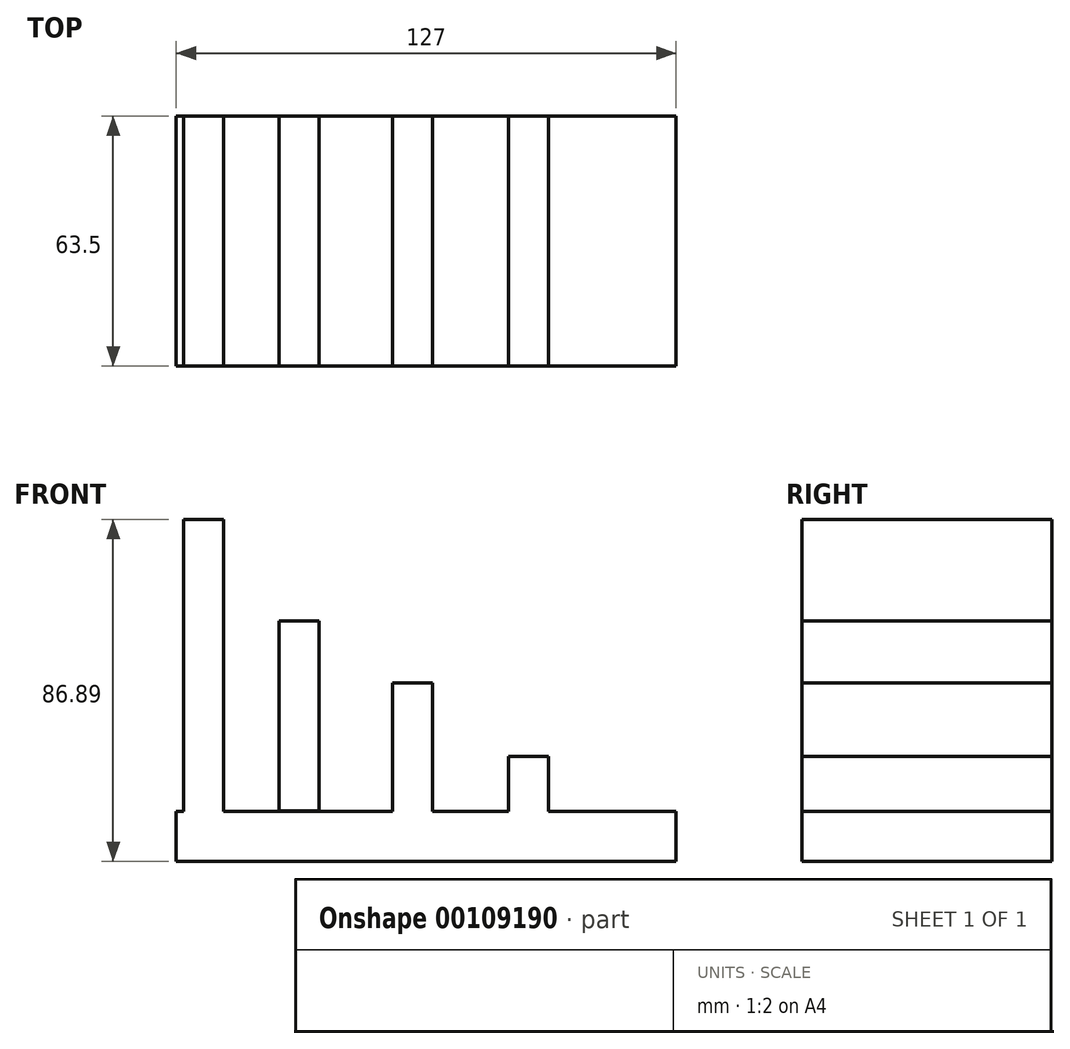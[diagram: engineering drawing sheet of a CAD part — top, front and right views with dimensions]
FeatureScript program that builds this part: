
annotation { "Feature Type Name" : "Feature", "Feature Type Description" : "" }
export const myFeature = defineFeature(function(context is Context, id is Id, definition is map)
    precondition{}
    {
        {
            var Q0;
            Q0=qCreatedBy(makeId("Front.planeOp"),FACE);
            var sketch = newSketch(context, id + "F0", { "sketchPlane" : qUnion([Q0])});
            skLineSegment(sketch, "E0.bottom", {"start": v(-60.38, -31.27) * mm, "end": v(66.62, -31.27) * mm});
            skLineSegment(sketch, "E0.top", {"start": v(-60.38, -43.97) * mm, "end": v(66.62, -43.97) * mm});
            skLineSegment(sketch, "E0.left", {"start": v(-60.38, -31.27) * mm, "end": v(-60.38, -43.97) * mm});
            skLineSegment(sketch, "E0.right", {"start": v(66.62, -31.27) * mm, "end": v(66.62, -43.97) * mm});
            skSolve(sketch);
        }
        {
            var Q0;
            Q0=qCreatedBy(makeId("Front.planeOp"),FACE);
            var sketch = newSketch(context, id + "F1", { "sketchPlane" : qUnion([Q0])});
            skLineSegment(sketch, "E1.bottom", {"start": v(-58.53, -33.29) * mm, "end": v(-48.37, -33.29) * mm});
            skLineSegment(sketch, "E1.top", {"start": v(-58.53, 42.92) * mm, "end": v(-48.37, 42.92) * mm});
            skLineSegment(sketch, "E1.left", {"start": v(-58.53, -33.29) * mm, "end": v(-58.53, 42.92) * mm});
            skLineSegment(sketch, "E1.right", {"start": v(-48.37, -33.29) * mm, "end": v(-48.37, 42.92) * mm});
            skFitSpline(sketch, "E2", {"points": [v(-48.37, 42.92) * mm, v(53.2, -35.52) * mm], "startDerivative": vector(74.92, -128.75) * mm, "endDerivative": vector(141.8, -32.15) * mm});
            skSolve(sketch);
        }
        {
            var Q0;
            Q0=makeQuery(id+"F0.imprint","IMPRINT",FACE,{"disambiguationData":[TD([[makeQuery(id+"F0.imprint","IMPRINT",EDGE,{"derivedFrom":sQuery(id+"F0.wireOp",EDGE,"E0.bottom")}),-1.0]])]});
            extrude(context, id + "F2", {"entities" : qUnion([Q0]), "depth" : 63.5 * mm});
        }
        {
            var Q0;
            Q0=makeQuery(id+"F1.imprint","IMPRINT",FACE,{"disambiguationData":[TD([[makeQuery(id+"F1.imprint","IMPRINT",EDGE,{"derivedFrom":sQuery(id+"F1.wireOp",EDGE,"E1.bottom")}),1.0]])]});
            extrude(context, id + "F3", {"entities" : qUnion([Q0]), "operationType" : NewBodyOperationType.ADD, "depth" : 63.5 * mm});
        }
        {
            var Q0;
            Q0=qCreatedBy(makeId("Front.planeOp"),FACE);
            var sketch = newSketch(context, id + "F4", { "sketchPlane" : qUnion([Q0])});
            skLineSegment(sketch, "E3.bottom", {"start": v(-34.2, -31.15) * mm, "end": v(-24.05, -31.15) * mm});
            skLineSegment(sketch, "E3.top", {"start": v(-34.2, 17.11) * mm, "end": v(-24.05, 17.11) * mm});
            skLineSegment(sketch, "E3.left", {"start": v(-34.2, -31.15) * mm, "end": v(-34.2, 17.11) * mm});
            skLineSegment(sketch, "E3.right", {"start": v(-24.05, -31.15) * mm, "end": v(-24.05, 17.11) * mm});
            skSolve(sketch);
        }
        {
            var Q0;
            Q0=qCreatedBy(makeId("Front.planeOp"),FACE);
            var sketch = newSketch(context, id + "F5", { "sketchPlane" : qUnion([Q0])});
            skLineSegment(sketch, "E4.bottom", {"start": v(-5.4, -31.66) * mm, "end": v(4.77, -31.66) * mm});
            skLineSegment(sketch, "E4.top", {"start": v(-5.4, 1.36) * mm, "end": v(4.77, 1.36) * mm});
            skLineSegment(sketch, "E4.left", {"start": v(-5.4, -31.66) * mm, "end": v(-5.4, 1.36) * mm});
            skLineSegment(sketch, "E4.right", {"start": v(4.77, -31.66) * mm, "end": v(4.77, 1.36) * mm});
            skSolve(sketch);
        }
        {
            var Q0;
            Q0=qCreatedBy(makeId("Front.planeOp"),FACE);
            var sketch = newSketch(context, id + "F6", { "sketchPlane" : qUnion([Q0])});
            skLineSegment(sketch, "E5.bottom", {"start": v(24.09, -32.48) * mm, "end": v(34.25, -32.48) * mm});
            skLineSegment(sketch, "E5.top", {"start": v(24.09, -17.24) * mm, "end": v(34.25, -17.24) * mm});
            skLineSegment(sketch, "E5.left", {"start": v(24.09, -32.48) * mm, "end": v(24.09, -17.24) * mm});
            skLineSegment(sketch, "E5.right", {"start": v(34.25, -32.48) * mm, "end": v(34.25, -17.24) * mm});
            skSolve(sketch);
        }
        {
            var Q0;
            Q0 = qSketchRegion(id + "F4", true);
            extrude(context, id + "F7", {"entities" : qUnion([Q0]), "depth" : 63.5 * mm});
        }
        {
            var Q0;
            Q0=makeQuery(id+"F5.imprint","IMPRINT",FACE,{"disambiguationData":[TD([[makeQuery(id+"F5.imprint","IMPRINT",EDGE,{"derivedFrom":sQuery(id+"F5.wireOp",EDGE,"E4.bottom")}),1.0]])]});
            extrude(context, id + "F8", {"entities" : qUnion([Q0]), "operationType" : NewBodyOperationType.ADD, "depth" : 63.5 * mm});
        }
        {
            var Q0;
            Q0=makeQuery(id+"F6.imprint","IMPRINT",FACE,{"disambiguationData":[TD([[makeQuery(id+"F6.imprint","IMPRINT",EDGE,{"derivedFrom":sQuery(id+"F6.wireOp",EDGE,"E5.bottom")}),1.0]])]});
            extrude(context, id + "F9", {"entities" : qUnion([Q0]), "operationType" : NewBodyOperationType.ADD, "depth" : 63.5 * mm});
        }
    });
